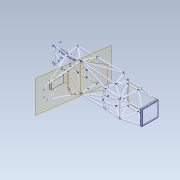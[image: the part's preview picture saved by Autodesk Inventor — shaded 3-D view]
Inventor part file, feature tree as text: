
AUTODESK INVENTOR PART (.ipt)
format: ipt  version: 2021 (Build 250183000, 183)  size: 2,531,840 bytes
history: mixed  units: in
note: dims shown in document units (in); Inventor stores cm internally (conversion verified against a paired STEP export)
features: surface_op x65, other x21, mirror x10, boolean_combine x6, plane x1, imported_body x1
ambient origin geometry x8: Origin, YZ Plane, XZ Plane, XY Plane, X Axis, Y Axis, Z Axis, Center Point
bodies: Solid1 (imported_parasolid), Solid2 (imported_parasolid), Solid3 (imported_parasolid), Solid4 (imported_parasolid), Solid5 (imported_parasolid), Solid6 (imported_parasolid), Solid7 (imported_parasolid), Solid8 (imported_parasolid), Solid9 (imported_parasolid), Solid10 (imported_parasolid), Solid11 (imported_parasolid), Solid12 (imported_parasolid), Solid13 (imported_parasolid), Solid14 (imported_parasolid), Solid15 (imported_parasolid), Solid16 (imported_parasolid), Solid17 (imported_parasolid), Solid18 (imported_parasolid), Solid19 (imported_parasolid), Solid20 (imported_parasolid), Solid21 (imported_parasolid), Solid22 (imported_parasolid), Solid23 (imported_parasolid), Solid24 (imported_parasolid), Solid25 (imported_parasolid), Solid26 (imported_parasolid), Solid27 (imported_parasolid), Solid28 (imported_parasolid), Solid29 (imported_parasolid), Solid30 (imported_parasolid), Solid31 (imported_parasolid), Solid32 (imported_parasolid), Solid33 (imported_parasolid), Solid34 (imported_parasolid), Solid35 (imported_parasolid), Solid36 (imported_parasolid), Solid37 (imported_parasolid), Solid38 (imported_parasolid), Solid39 (imported_parasolid), Solid40 (imported_parasolid), Solid41 (imported_parasolid), Solid42 (imported_parasolid), Solid43 (imported_parasolid), Solid44 (imported_parasolid), Solid45 (imported_parasolid), Solid46 (imported_parasolid), Solid47 (imported_parasolid), Solid48 (imported_parasolid), Solid49 (imported_parasolid), Solid50 (imported_parasolid), Solid51 (imported_parasolid), Solid52 (imported_parasolid), Solid53 (imported_parasolid), Solid54 (imported_parasolid), Solid55 (imported_parasolid), Solid56 (imported_parasolid), Solid57 (imported_parasolid), Solid58 (imported_parasolid), Solid59 (imported_parasolid), Solid60 (imported_parasolid), Solid61 (imported_parasolid), Solid62 (imported_parasolid), Solid63 (imported_parasolid), Solid64 (imported_parasolid), Solid65 (imported_parasolid), Solid66 (imported_parasolid), Solid67 (imported_parasolid), Solid68 (imported_parasolid), Solid69 (imported_parasolid), Solid70 (imported_parasolid), Solid71 (imported_parasolid), Solid72 (imported_parasolid), Solid73 (imported_parasolid), Solid74 (imported_parasolid), Solid75 (imported_parasolid), Solid76 (imported_parasolid), Solid77 (imported_parasolid), Solid78 (imported_parasolid), Solid79 (imported_parasolid), Solid80 (imported_parasolid), Solid81 (imported_parasolid), Solid82 (imported_parasolid), Solid83 (imported_parasolid), Solid84 (imported_parasolid), Solid85 (imported_parasolid), Solid86 (imported_parasolid), Solid87 (imported_parasolid), Solid88 (imported_parasolid), Solid89 (imported_parasolid), Solid90 (imported_parasolid), Solid91 (imported_parasolid), Solid92 (imported_parasolid), Solid93 (imported_parasolid), Solid94 (imported_parasolid), Solid95 (imported_parasolid), Solid96 (imported_parasolid), Solid97 (imported_parasolid), Solid98 (imported_parasolid), Solid99 (imported_parasolid), Solid100 (imported_parasolid)
feature tree (104):
  plane  "Work Plane1"
  surface_op  "Trim_Extend2"
  boolean_combine  "Combine1"
  other  "Al tube (square) 1 SQ X .049 WALL(10)[1]"
  other  "Al tube (square) 1 SQ X .049 WALL(10)[2]"
  other  "Al tube (square) 1 SQ X .049 WALL(10)[3]"
  other  "Al tube (square) 1 SQ X .049 WALL(10)[4]"
  other  "Al round tubing 1 OD X 0.049 WALL(1)[2]"
  other  "Al round tubing 1 OD X 0.049 WALL(1)[4]"
  surface_op  "Trim_Extend5[1]"
  surface_op  "Trim_Extend5[2]"
  surface_op  "Trim_Extend7[1]"
  surface_op  "Trim_Extend7[2]"
  surface_op  "Trim_Extend23[1]"
  surface_op  "Trim_Extend23[2]"
  surface_op  "Trim_Extend23[3]"
  surface_op  "Trim_Extend23[4]"
  surface_op  "Trim_Extend62[1]"
  surface_op  "Trim_Extend62[2]"
  surface_op  "Trim_Extend63[1]"
  surface_op  "Trim_Extend63[2]"
  surface_op  "Trim_Extend64[1]"
  surface_op  "Trim_Extend64[2]"
  surface_op  "Trim_Extend75[1]"
  surface_op  "Trim_Extend75[2]"
  surface_op  "Trim_Extend74[1]"
  surface_op  "Trim_Extend74[2]"
  surface_op  "Trim_Extend70[1]"
  surface_op  "Trim_Extend70[2]"
  surface_op  "Trim_Extend69[1]"
  surface_op  "Trim_Extend69[2]"
  surface_op  "Trim_Extend67"
  surface_op  "Trim_Extend76[1]"
  surface_op  "Trim_Extend76[2]"
  surface_op  "Trim_Extend79[1]"
  surface_op  "Trim_Extend79[2]"
  other  "AIP Plate -1.5mm"
  boolean_combine  "Combine3"
  surface_op  "Trim_Extend14"
  surface_op  "Trim_Extend15"
  surface_op  "Trim_Extend16[1]"
  surface_op  "Trim_Extend16[2]"
  surface_op  "Trim_Extend17[1]"
  surface_op  "Trim_Extend17[2]"
  surface_op  "Trim_Extend18[1]"
  surface_op  "Trim_Extend18[2]"
  surface_op  "Trim_Extend19[1]"
  surface_op  "Trim_Extend19[2]"
  surface_op  "Trim_Extend20[1]"
  surface_op  "Trim_Extend20[2]"
  other  "Boss-Extrude9"
  other  "Al round tubing 1.125 OD X 0.063 WALL(1)"
  surface_op  "Trim_Extend38[1]"
  surface_op  "Trim_Extend80"
  other  "Al tube (rectangular) 2.00 X 1.00 RECT X .104 WALL(18)[2]"
  surface_op  "Trim_Extend31"
  surface_op  "Trim_Extend32"
  surface_op  "Trim_Extend33"
  surface_op  "Trim_Extend30[1]"
  surface_op  "Trim_Extend30[2]"
  mirror  "Mirror1[1]"
  mirror  "Mirror1[2]"
  mirror  "Mirror1[3]"
  mirror  "Mirror1[5]"
  mirror  "Mirror1[6]"
  other  "Fsae 1 OD X 0.049 WALL(9)"
  surface_op  "Trim_Extend26"
  other  "JackbarCloseoutPlate"
  surface_op  "Trim_Extend29[1]"
  surface_op  "Trim_Extend29[2]"
  boolean_combine  "Combine9"
  surface_op  "Trim_Extend34"
  surface_op  "Trim_Extend35[1]"
  surface_op  "Trim_Extend35[2]"
  mirror  "Mirror2[1]"
  mirror  "Mirror2[2]"
  mirror  "Mirror2[3]"
  surface_op  "Trim_Extend41"
  surface_op  "Trim_Extend43[1]"
  surface_op  "Trim_Extend43[2]"
  surface_op  "Trim_Extend42[1]"
  surface_op  "Trim_Extend42[2]"
  surface_op  "Trim_Extend36"
  other  "Headrest"
  surface_op  "Trim_Extend37[1]"
  surface_op  "Trim_Extend37[2]"
  surface_op  "Trim_Extend37[3]"
  other  "Boss-Extrude6"
  surface_op  "Trim_Extend53"
  mirror  "Mirror3"
  other  "Boss-Extrude8"
  mirror  "Mirror5"
  surface_op  "Trim_Extend49[1]"
  surface_op  "Trim_Extend49[2]"
  other  "Split2[3]"
  other  "Split3[2]"
  boolean_combine  "Combine10"
  boolean_combine  "Combine11"
  boolean_combine  "Combine12"
  other  "Move Face1"
  other  "Move Face2"
  other  "Composite1"
  other  "Srf1"
  imported_body  NMx_Import_Brep_tag  [imported B-rep: ~205 faces, bbox_mm=[33.250843, 287.337139, 71.20858]]
